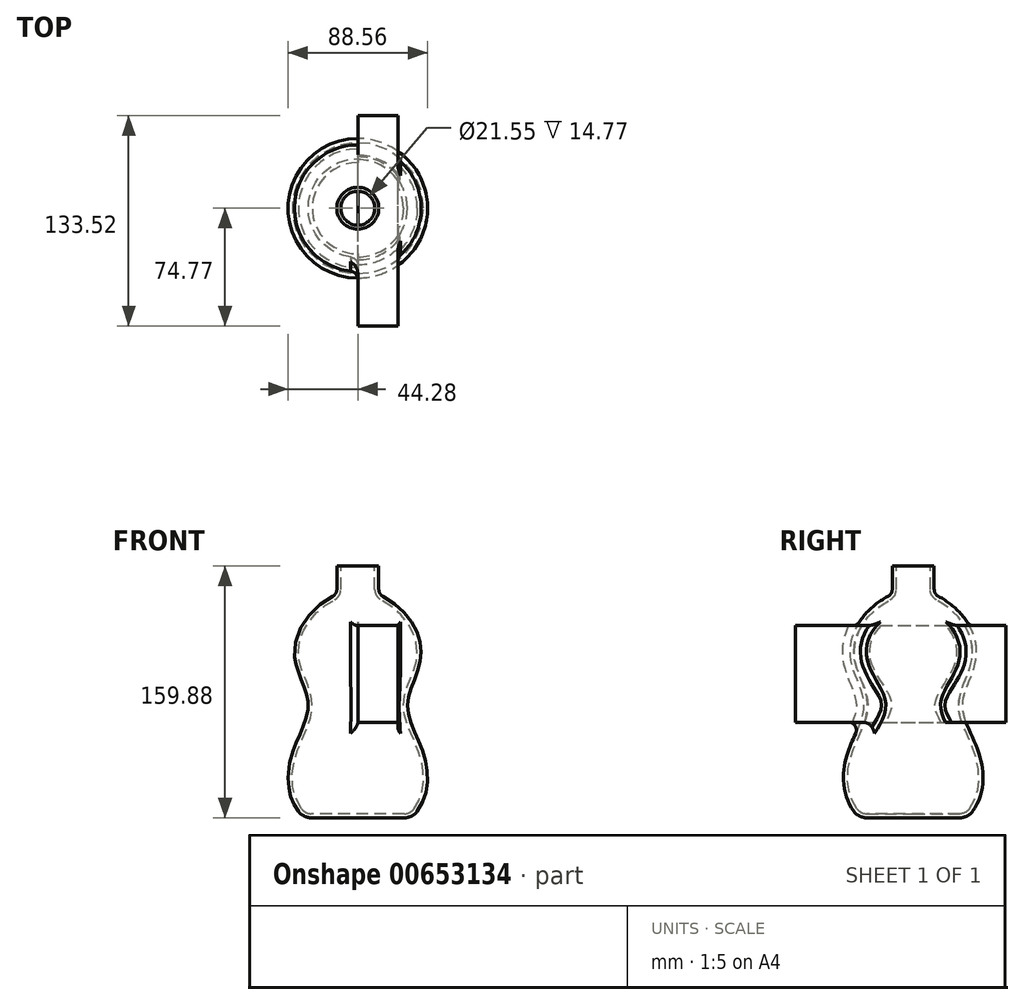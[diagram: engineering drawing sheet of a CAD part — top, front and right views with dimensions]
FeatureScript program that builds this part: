
annotation { "Feature Type Name" : "Feature", "Feature Type Description" : "" }
export const myFeature = defineFeature(function(context is Context, id is Id, definition is map)
    precondition{}
    {
        {
            var Q0;
            Q0=qCreatedBy(makeId("Front.planeOp"),FACE);
            var sketch = newSketch(context, id + "F0", { "sketchPlane" : qUnion([Q0])});
            skLineSegment(sketch, "E0", {"start": v(0, 0) * mm, "end": v(34.05, 0) * mm});
            skFitSpline(sketch, "E1", {"points": [v(34.05, 0) * mm, v(42.42, 38.4) * mm, v(31.44, 71.83) * mm, v(40.2, 103.1) * mm, v(13.31, 141.98) * mm], "startDerivative": vector(128.56, 120.56) * mm, "endDerivative": vector(-204.83, 96.82) * mm});
            skLineSegment(sketch, "E2", {"start": v(13.31, 141.98) * mm, "end": v(13.31, 159.88) * mm});
            skLineSegment(sketch, "E3", {"start": v(13.31, 159.88) * mm, "end": v(0, 159.88) * mm});
            skLineSegment(sketch, "E4", {"start": v(0, 159.88) * mm, "end": v(0, 0) * mm});
            skSolve(sketch);
        }
        {
            var Q0;
            Q0=makeQuery(id+"F0.imprint","IMPRINT",FACE,{"disambiguationData":[TD([[makeQuery(id+"F0.imprint","IMPRINT",EDGE,{"derivedFrom":sQuery(id+"F0.wireOp",EDGE,"E0")}),1.0]])]});
            var Q1;
            Q1=sQuery(id+"F0.wireOp",EDGE,"E4");
            revolve(context, id + "F1", {"entities" : qUnion([Q0]), "axis" : qUnion([Q1]), "revolveType" : RevolveType.FULL});
        }
        {
            var Q0;
            Q0=makeQuery(id+"F1.opRevolve","SWEPT_EDGE",EDGE,{"disambiguationData":[OSD([sQuery(id+"F0.wireOp",EDGE,"E1"),sQuery(id+"F0.wireOp",EDGE,"E2")])]});
            fillet(context, id + "F2", {"entities" : qUnion([Q0]), "radius" : 5.08 * mm, "tangentPropagation" : true, "allowEdgeOverflow" : false});
        }
        {
            var Q0;
            Q0=makeQuery(id+"F1.opRevolve","SWEPT_EDGE",EDGE,{"disambiguationData":[OSD([sQuery(id+"F0.wireOp",EDGE,"E0"),sQuery(id+"F0.wireOp",EDGE,"E1")])]});
            fillet(context, id + "F3", {"entities" : qUnion([Q0]), "radius" : 10.16 * mm, "tangentPropagation" : true, "allowEdgeOverflow" : false});
        }
        {
            var Q0;
            Q0=makeQuery(id+"F1.opRevolve","SWEPT_FACE",FACE,{"disambiguationData":[OSD([sQuery(id+"F0.wireOp",EDGE,"E3")])]});
            shell(context, id + "F4", {"entities" : qUnion([Q0]), "thickness" : 2.54 * mm});
        }
        {
            var Q0;
            Q0=qCreatedBy(makeId("Right.planeOp"),FACE);
            var sketch = newSketch(context, id + "F5", { "sketchPlane" : qUnion([Q0])});
            skLineSegment(sketch, "E5.bottom", {"start": v(-74.77, 60.7) * mm, "end": v(58.75, 60.7) * mm});
            skLineSegment(sketch, "E5.top", {"start": v(-74.77, 122.05) * mm, "end": v(58.75, 122.05) * mm});
            skLineSegment(sketch, "E5.left", {"start": v(-74.77, 60.7) * mm, "end": v(-74.77, 122.05) * mm});
            skLineSegment(sketch, "E5.right", {"start": v(58.75, 60.7) * mm, "end": v(58.75, 122.05) * mm});
            skSolve(sketch);
        }
        {
            var Q0;
            Q0 = qSketchRegion(id + "F5", true);
            extrude(context, id + "F6", {"entities" : qUnion([Q0]), "operationType" : NewBodyOperationType.ADD, "depth" : 25.4 * mm, "offsetDistance" : 25.4 * mm});
        }
        {
            var Q0;
            Q0=makeQuery(id+"F6.boolean.opBoolean","INTERSECT",EDGE,{"disambiguationData":[OD(0.0)],"derivedFrom":[makeQuery(id+"F1.opRevolve","SWEPT_FACE",FACE,{"disambiguationData":[OSD([sQuery(id+"F0.wireOp",EDGE,"E1")])]}),makeQuery(id+"F6.opExtrude","CAP_FACE",FACE,{"disambiguationData":[OSD([sQuery(id+"F5.wireOp",EDGE,"E5.bottom"),sQuery(id+"F5.wireOp",EDGE,"E5.top"),sQuery(id+"F5.wireOp",EDGE,"E5.left"),sQuery(id+"F5.wireOp",EDGE,"E5.right")])],"isStart":false})]});
            var Q1;
            Q1=makeQuery(id+"F6.boolean.opBoolean","INTERSECT",EDGE,{"disambiguationData":[OD(1.0)],"derivedFrom":[makeQuery(id+"F1.opRevolve","SWEPT_FACE",FACE,{"disambiguationData":[OSD([sQuery(id+"F0.wireOp",EDGE,"E1")])]}),makeQuery(id+"F6.opExtrude","CAP_FACE",FACE,{"disambiguationData":[OSD([sQuery(id+"F5.wireOp",EDGE,"E5.bottom"),sQuery(id+"F5.wireOp",EDGE,"E5.top"),sQuery(id+"F5.wireOp",EDGE,"E5.left"),sQuery(id+"F5.wireOp",EDGE,"E5.right")])],"isStart":false})]});
            var Q2;
            Q2=makeQuery(id+"F6.boolean.opBoolean","INTERSECT",EDGE,{"disambiguationData":[OD(0.0)],"derivedFrom":[makeQuery(id+"F1.opRevolve","SWEPT_FACE",FACE,{"disambiguationData":[OSD([sQuery(id+"F0.wireOp",EDGE,"E1")])]}),makeQuery(id+"F6.opExtrude","SWEPT_FACE",FACE,{"disambiguationData":[OSD([sQuery(id+"F5.wireOp",EDGE,"E5.top")])]})]});
            var Q3;
            Q3=makeQuery(id+"F6.boolean.opBoolean","INTERSECT",EDGE,{"disambiguationData":[OD(1.0)],"derivedFrom":[makeQuery(id+"F1.opRevolve","SWEPT_FACE",FACE,{"disambiguationData":[OSD([sQuery(id+"F0.wireOp",EDGE,"E1")])]}),makeQuery(id+"F6.opExtrude","SWEPT_FACE",FACE,{"disambiguationData":[OSD([sQuery(id+"F5.wireOp",EDGE,"E5.top")])]})]});
            var Q4;
            Q4=makeQuery(id+"F6.boolean.opBoolean","INTERSECT",EDGE,{"disambiguationData":[OD(0.0)],"derivedFrom":[makeQuery(id+"F1.opRevolve","SWEPT_FACE",FACE,{"disambiguationData":[OSD([sQuery(id+"F0.wireOp",EDGE,"E1")])]}),makeQuery(id+"F6.opExtrude","CAP_FACE",FACE,{"disambiguationData":[OSD([sQuery(id+"F5.wireOp",EDGE,"E5.bottom"),sQuery(id+"F5.wireOp",EDGE,"E5.top"),sQuery(id+"F5.wireOp",EDGE,"E5.left"),sQuery(id+"F5.wireOp",EDGE,"E5.right")])],"isStart":true})]});
            var Q5;
            Q5=makeQuery(id+"F6.boolean.opBoolean","INTERSECT",EDGE,{"disambiguationData":[OD(0.0)],"derivedFrom":[makeQuery(id+"F1.opRevolve","SWEPT_FACE",FACE,{"disambiguationData":[OSD([sQuery(id+"F0.wireOp",EDGE,"E1")])]}),makeQuery(id+"F6.opExtrude","SWEPT_FACE",FACE,{"disambiguationData":[OSD([sQuery(id+"F5.wireOp",EDGE,"E5.bottom")])]})]});
            fillet(context, id + "F7", {"entities" : qUnion([Q0, Q1, Q2, Q3, Q4, Q5]), "radius" : 5.08 * mm, "tangentPropagation" : true, "allowEdgeOverflow" : false});
        }
    });
